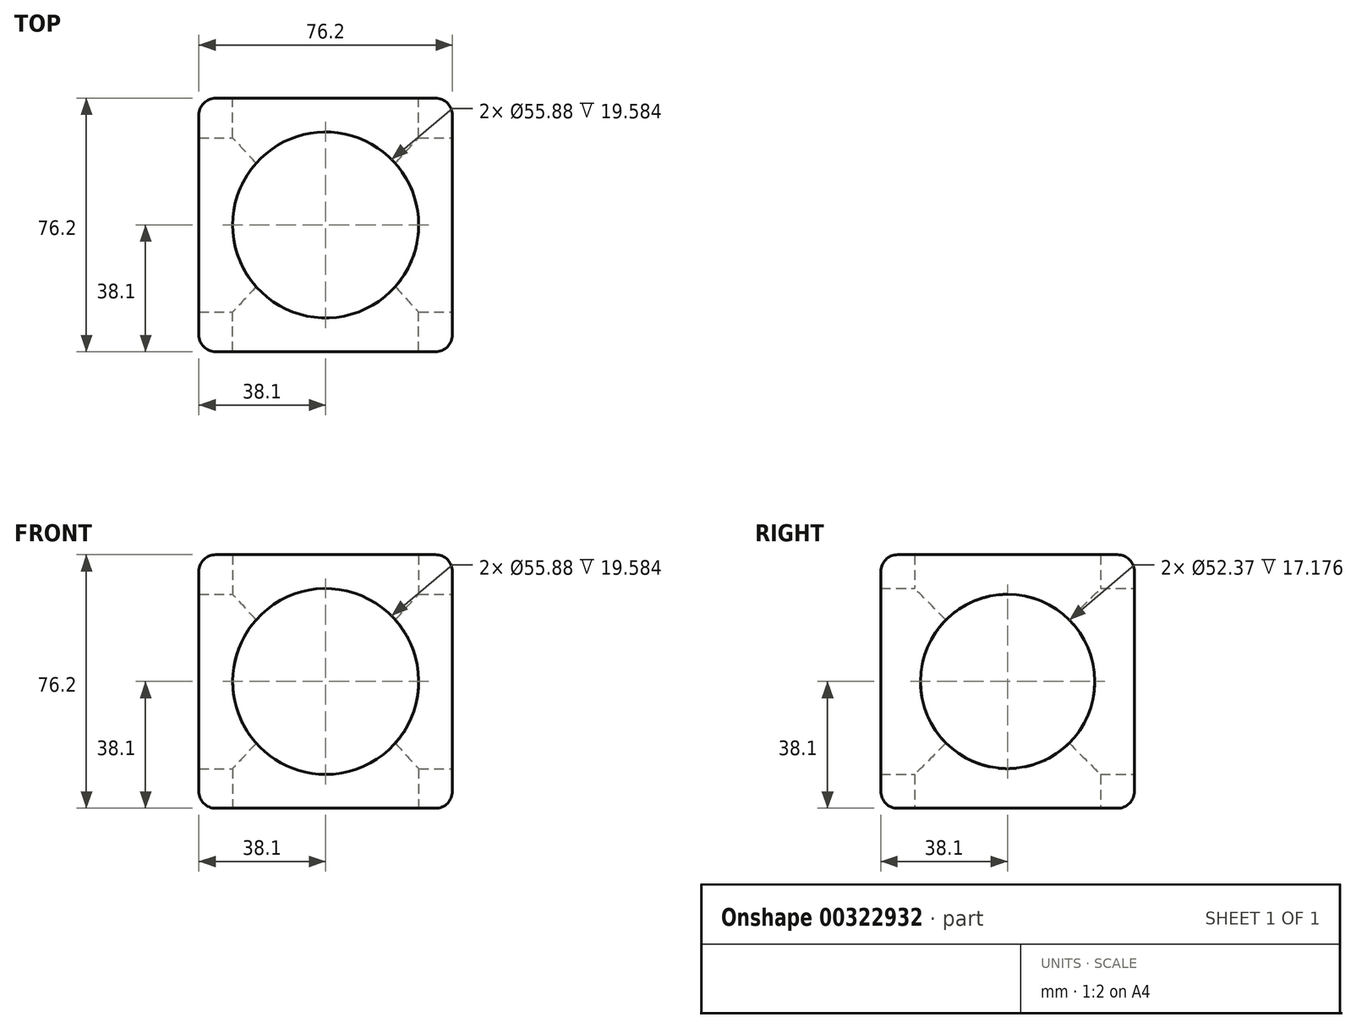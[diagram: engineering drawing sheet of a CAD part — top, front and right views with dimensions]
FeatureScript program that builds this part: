
annotation { "Feature Type Name" : "Feature", "Feature Type Description" : "" }
export const myFeature = defineFeature(function(context is Context, id is Id, definition is map)
    precondition{}
    {
        {
            var Q0;
            Q0=qCreatedBy(makeId("Top.planeOp"),FACE);
            var sketch = newSketch(context, id + "F0", { "sketchPlane" : qUnion([Q0])});
            skLineSegment(sketch, "E0.bottom", {"start": v(38.1, -38.1) * mm, "end": v(-38.1, -38.1) * mm});
            skLineSegment(sketch, "E0.top", {"start": v(38.1, 38.1) * mm, "end": v(-38.1, 38.1) * mm});
            skLineSegment(sketch, "E0.left", {"start": v(38.1, -38.1) * mm, "end": v(38.1, 38.1) * mm});
            skLineSegment(sketch, "E0.right", {"start": v(-38.1, -38.1) * mm, "end": v(-38.1, 38.1) * mm});
            skPoint(sketch, "E0.middle", {"position": v(0, 0) * mm});
            skSolve(sketch);
        }
        {
            var Q0;
            Q0=makeQuery(id+"F0.imprint","IMPRINT",FACE,{"disambiguationData":[TD([[makeQuery(id+"F0.imprint","IMPRINT",EDGE,{"derivedFrom":sQuery(id+"F0.wireOp",EDGE,"E0.bottom")}),-1.0]])]});
            extrude(context, id + "F1", {"entities" : qUnion([Q0]), "depth" : 76.2 * mm});
        }
        {
            var Q0;
            Q0=makeQuery(id+"F1.opExtrude","SWEPT_FACE",FACE,{"disambiguationData":[OSD([sQuery(id+"F0.wireOp",EDGE,"E0.bottom")])]});
            var Q1;
            Q1=makeQuery(id+"F1.opExtrude","SWEPT_FACE",FACE,{"disambiguationData":[OSD([sQuery(id+"F0.wireOp",EDGE,"E0.left")])]});
            var Q2;
            Q2=makeQuery(id+"F1.opExtrude","CAP_FACE",FACE,{"disambiguationData":[OSD([sQuery(id+"F0.wireOp",EDGE,"E0.bottom"),sQuery(id+"F0.wireOp",EDGE,"E0.top"),sQuery(id+"F0.wireOp",EDGE,"E0.left"),sQuery(id+"F0.wireOp",EDGE,"E0.right")])],"isStart":false});
            var Q3;
            Q3=makeQuery(id+"F1.opExtrude","SWEPT_FACE",FACE,{"disambiguationData":[OSD([sQuery(id+"F0.wireOp",EDGE,"E0.top")])]});
            var Q4;
            Q4=makeQuery(id+"F1.opExtrude","SWEPT_FACE",FACE,{"disambiguationData":[OSD([sQuery(id+"F0.wireOp",EDGE,"E0.right")])]});
            var Q5;
            Q5=makeQuery(id+"F1.opExtrude","CAP_FACE",FACE,{"disambiguationData":[OSD([sQuery(id+"F0.wireOp",EDGE,"E0.bottom"),sQuery(id+"F0.wireOp",EDGE,"E0.top"),sQuery(id+"F0.wireOp",EDGE,"E0.left"),sQuery(id+"F0.wireOp",EDGE,"E0.right")])],"isStart":true});
            fillet(context, id + "F2", {"entities" : qUnion([Q0, Q1, Q2, Q3, Q4, Q5]), "radius" : 5.08 * mm, "tangentPropagation" : true, "allowEdgeOverflow" : false});
        }
        {
            var Q0;
            Q0=makeQuery(id+"F1.opExtrude","CAP_FACE",FACE,{"disambiguationData":[OSD([sQuery(id+"F0.wireOp",EDGE,"E0.bottom"),sQuery(id+"F0.wireOp",EDGE,"E0.top"),sQuery(id+"F0.wireOp",EDGE,"E0.left"),sQuery(id+"F0.wireOp",EDGE,"E0.right")])],"isStart":true});
            var sketch = newSketch(context, id + "F3", { "sketchPlane" : qUnion([Q0])});
            skCircle(sketch, "E1", {"center": v(0, 0) * mm, "radius": 27.94 * mm});
            skSolve(sketch);
        }
        {
            var Q0;
            Q0=makeQuery(id+"F3.imprint","IMPRINT",FACE,{"disambiguationData":[TD([[makeQuery(id+"F3.imprint","IMPRINT",EDGE,{"derivedFrom":sQuery(id+"F3.wireOp",EDGE,"E1")}),1.0]])]});
            extrude(context, id + "F4", {"entities" : qUnion([Q0]), "operationType" : NewBodyOperationType.REMOVE, "oppositeDirection" : true, "depth" : 83.82 * mm});
        }
        {
            var Q0;
            Q0=makeQuery(id+"F1.opExtrude","SWEPT_FACE",FACE,{"disambiguationData":[OSD([sQuery(id+"F0.wireOp",EDGE,"E0.left")])]});
            var sketch = newSketch(context, id + "F5", { "sketchPlane" : qUnion([Q0])});
            skLineSegment(sketch, "E2", {"start": v(33.02, 71.12) * mm, "end": v(-33.02, 5.08) * mm, "construction": true});
            skLineSegment(sketch, "E3", {"start": v(-33.02, 71.12) * mm, "end": v(33.02, 5.08) * mm, "construction": true});
            skCircle(sketch, "E4", {"center": v(0, 38.1) * mm, "radius": 26.19 * mm});
            skSolve(sketch);
        }
        {
            var Q0;
            Q0 = qSketchRegion(id + "F5", true);
            extrude(context, id + "F6", {"entities" : qUnion([Q0]), "operationType" : NewBodyOperationType.REMOVE, "oppositeDirection" : true, "depth" : 78.74 * mm});
        }
        {
            var Q0;
            Q0=makeQuery(id+"F1.opExtrude","SWEPT_FACE",FACE,{"disambiguationData":[OSD([sQuery(id+"F0.wireOp",EDGE,"E0.top")])]});
            var sketch = newSketch(context, id + "F7", { "sketchPlane" : qUnion([Q0])});
            skLineSegment(sketch, "E5", {"start": v(33.02, 71.12) * mm, "end": v(-33.02, 5.08) * mm, "construction": true});
            skLineSegment(sketch, "E6", {"start": v(-33.02, 71.12) * mm, "end": v(33.02, 5.08) * mm, "construction": true});
            skCircle(sketch, "E7", {"center": v(0, 38.1) * mm, "radius": 27.94 * mm});
            skSolve(sketch);
        }
        {
            var Q0;
            Q0 = qSketchRegion(id + "F7", true);
            extrude(context, id + "F8", {"entities" : qUnion([Q0]), "operationType" : NewBodyOperationType.REMOVE, "oppositeDirection" : true, "depth" : 78.74 * mm});
        }
    });
